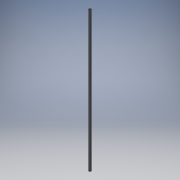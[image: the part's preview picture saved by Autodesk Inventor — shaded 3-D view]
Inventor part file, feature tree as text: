
AUTODESK INVENTOR PART (.ipt)
format: ipt  version: 2018 (Build 220112000, 112)  size: 103,424 bytes
history: native  units: mm
features: other x1, extrude x1, sketch x1
ambient origin geometry x8: Origin, YZ Plane, XZ Plane, XY Plane, X Axis, Y Axis, Z Axis, Center Point
bodies: Solid1 (feature_tree)
feature tree (3):
  parser-record x1  (decoder bookkeeping rows leaked as tree rows — omitted from the tree; the rows remain in map.json)
  extrude  "Extrusion1"  Depth=1884.0mm
  sketch  "Sketch1"  dims[d0=3.2mm d1=33.7mm d2=27.3mm d3=1884.0mm d4=0.0mm]
note: 1 file-system path scrubbed to <path> (originals preserved in map.json)
